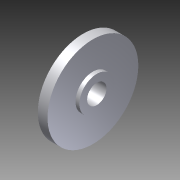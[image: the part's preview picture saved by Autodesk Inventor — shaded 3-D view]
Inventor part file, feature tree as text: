
AUTODESK INVENTOR PART (.ipt)
format: ipt  version: 2012 (Build 160160000, 160)  size: 606,720 bytes
history: native  units: in
note: dims shown in document units (in); Inventor stores cm internally (conversion verified against a paired STEP export)
features: extrude x3, sketch x1, imported_body x1
ambient origin geometry x8: Origin, YZ Plane, XZ Plane, XY Plane, X Axis, Y Axis, Z Axis, Center Point
feature tree (5):
  sketch  "Sketch1"  dims[d0=0.375in d3=0.3in d4=0.0in d5=1.0in d6=0.125in d7=0.125in d8=0.0625in d9=0.5625in d10=0.3in d11=0.0in d12=1.75in d13=1.0in d14=0.0in]
  extrude  "Extrusion2"  Depth=0.3in TaperAngle=0.0deg
  extrude  "Extrusion3"  Depth=1.0in
  extrude  "Extrusion4"  Depth=0.125in
  imported_body  "Base1"
